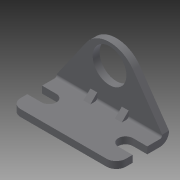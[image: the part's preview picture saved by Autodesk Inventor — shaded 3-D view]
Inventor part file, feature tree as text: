
AUTODESK INVENTOR PART (.ipt)
format: ipt  version: 2013 (Build 170138000, 138)  size: 189,952 bytes
history: native  units: in
note: dims shown in document units (in); Inventor stores cm internally (conversion verified against a paired STEP export)
features: other x126, sketch x9, extrude x8, hole x1
ambient origin geometry x8: Origin, YZ Plane, XZ Plane, XY Plane, X Axis, Y Axis, Z Axis, Center Point
bodies: Solid1 (feature_tree)
feature tree (144):
  extrude  "Extrusion1"  Depth=0.1346in TaperAngle=0.0deg
  extrude  "Extrusion2"  Depth=0.1346in TaperAngle=0.0deg
  hole  "Drilling 1"  [1 undecoded]
  extrude  "Extrusion3"  Depth=0.0897in TaperAngle=0.0deg
  extrude  "Extrusion4"  [1 undecoded]
  extrude  "Extrusion5"  [1 undecoded]
  extrude  "Extrusion6"  [1 undecoded]
  extrude  "Extrusion7"  [1 undecoded]
  extrude  "Extrusion8"  [1 undecoded]
  other  "h1_XY"
  other  "h1_YZ"
  other  "h1_ZX"
  other  "h1_X"
  other  "h1_Y"
  other  "h1_Z"
  other  "h1_Center"
  other  "d1_XY"
  other  "d1_YZ"
  other  "d1_ZX"
  other  "d1_X"
  other  "d1_Y"
  other  "d1_Z"
  other  "d1_Center"
  other  "h2_XY"
  other  "h2_YZ"
  other  "h2_ZX"
  other  "h2_X"
  other  "h2_Y"
  other  "h2_Z"
  other  "h2_Center"
  other  "d2_XY"
  other  "d2_YZ"
  other  "d2_ZX"
  other  "d2_X"
  other  "d2_Y"
  other  "d2_Z"
  other  "d2_Center"
  other  "h3_XY"
  other  "h3_YZ"
  other  "h3_ZX"
  other  "h3_X"
  other  "h3_Y"
  other  "h3_Z"
  other  "h3_Center"
  other  "h4_XY"
  other  "h4_YZ"
  other  "h4_ZX"
  other  "h4_X"
  other  "h4_Y"
  other  "h4_Z"
  other  "h4_Center"
  other  "h5_XY"
  other  "h5_YZ"
  other  "h5_ZX"
  other  "h5_X"
  other  "h5_Y"
  other  "h5_Z"
  other  "h5_Center"
  other  "h6_XY"
  other  "h6_YZ"
  other  "h6_ZX"
  other  "h6_X"
  other  "h6_Y"
  other  "h6_Z"
  other  "h6_Center"
  other  "l1_XY"
  other  "l1_YZ"
  other  "l1_ZX"
  other  "l1_X"
  other  "l1_Y"
  other  "l1_Z"
  other  "l1_Center"
  other  "l2_XY"
  other  "l2_YZ"
  other  "l2_ZX"
  other  "l2_X"
  other  "l2_Y"
  other  "l2_Z"
  other  "l2_Center"
  other  "l3_XY"
  other  "l3_YZ"
  other  "l3_ZX"
  other  "l3_X"
  other  "l3_Y"
  other  "l3_Z"
  other  "l3_Center"
  other  "l4_XY"
  other  "l4_YZ"
  other  "l4_ZX"
  other  "l4_X"
  other  "l4_Y"
  other  "l4_Z"
  other  "l4_Center"
  other  "l5_XY"
  other  "l5_YZ"
  other  "l5_ZX"
  other  "l5_X"
  other  "l5_Y"
  other  "l5_Z"
  other  "l5_Center"
  other  "l6_XY"
  other  "l6_YZ"
  other  "l6_ZX"
  other  "l6_X"
  other  "l6_Y"
  other  "l6_Z"
  other  "l6_Center"
  other  "l7_XY"
  other  "l7_YZ"
  other  "l7_ZX"
  other  "l7_X"
  other  "l7_Y"
  other  "l7_Z"
  other  "l7_Center"
  other  "l8_XY"
  other  "l8_YZ"
  other  "l8_ZX"
  other  "l8_X"
  other  "l8_Y"
  other  "l8_Z"
  other  "l8_Center"
  other  "mounting_bracket_XY"
  other  "mounting_bracket_YZ"
  other  "mounting_bracket_ZX"
  other  "mounting_bracket_X"
  other  "mounting_bracket_Y"
  other  "mounting_bracket_Z"
  other  "mounting_bracket_Center"
  other  "mounting_bracket_1_XY"
  other  "mounting_bracket_1_YZ"
  other  "mounting_bracket_1_ZX"
  other  "mounting_bracket_1_X"
  other  "mounting_bracket_1_Y"
  other  "mounting_bracket_1_Z"
  other  "mounting_bracket_1_Center"
  sketch  "Sketch_1"  dims[d0=1.375in d1=0.0in d2=0.1346in d3=0.0in]
  sketch  "Sketch_2"  dims[d4=0.4405in d5=0.75in d6=0.375in d7=0.25in d8=0.5635in d9=0.1346in d10=0.0in d11=0.1346in d12=0.0in]
  sketch  "Sketch3"  dims[d13=0.1346in d14=0.0in d15=0.1346in d16=0.0in]
  sketch  "Sketch_6"  dims[d17=0.1346in d18=0.0in d19=0.0897in d20=0.0in]
  sketch  "Sketch_7"  dims[d21=0.0897in d22=0.0in]
  sketch  "Sketch_8"
  sketch  "Sketch_9"
  sketch  "Sketch_10"
  sketch  "Sketch_14"
note: 6 required parameter values undecoded (feature->parameter linkage not recoverable at this tier; creation-order binding heuristic only, values carry confidence <= 0.55)
